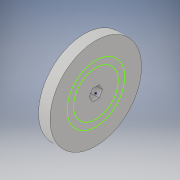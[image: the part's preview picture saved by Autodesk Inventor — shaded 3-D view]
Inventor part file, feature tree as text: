
AUTODESK INVENTOR PART (.ipt)
format: ipt  version: 2018 (Build 220112000, 112)  size: 103,936 bytes
history: native  units: in
note: dims shown in document units (in); Inventor stores cm internally (conversion verified against a paired STEP export)
features: sketch x2, extrude x1
ambient origin geometry x8: Origin, YZ Plane, XZ Plane, XY Plane, X Axis, Y Axis, Z Axis, Center Point
bodies: Solid1 (feature_tree)
feature tree (3):
  extrude  "Extrusion1"  Depth=0.5in
  sketch  "Sketch2"  dims[d2=0.5in d3=0.0in]
  sketch  "Sketch1"  dims[d0=3.98in d1=0.5in]
